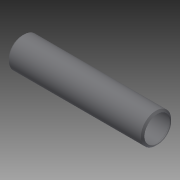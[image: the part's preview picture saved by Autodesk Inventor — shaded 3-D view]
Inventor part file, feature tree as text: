
AUTODESK INVENTOR PART (.ipt)
format: ipt  version: 2014 (Build 180170000, 170)  size: 122,368 bytes
history: native  units: in
note: dims shown in document units (in); Inventor stores cm internally (conversion verified against a paired STEP export)
features: other x56, revolve x1, sketch x1
ambient origin geometry x8: Origin, YZ Plane, XZ Plane, XY Plane, X Axis, Y Axis, Z Axis, Center Point
bodies: Solid1 (feature_tree)
feature tree (58):
  revolve  "Revolution1"  [1 undecoded]
  other  "o1_XY"
  other  "o1_YZ"
  other  "o1_ZX"
  other  "o1_X"
  other  "o1_Y"
  other  "o1_Z"
  other  "o1_Center"
  other  "o2_XY"
  other  "o2_YZ"
  other  "o2_ZX"
  other  "o2_X"
  other  "o2_Y"
  other  "o2_Z"
  other  "o2_Center"
  other  "t1_XY"
  other  "t1_YZ"
  other  "t1_ZX"
  other  "t1_X"
  other  "t1_Y"
  other  "t1_Z"
  other  "t1_Center"
  other  "t2_XY"
  other  "t2_YZ"
  other  "t2_ZX"
  other  "t2_X"
  other  "t2_Y"
  other  "t2_Z"
  other  "t2_Center"
  other  "t3_XY"
  other  "t3_YZ"
  other  "t3_ZX"
  other  "t3_X"
  other  "t3_Y"
  other  "t3_Z"
  other  "t3_Center"
  other  "t4_XY"
  other  "t4_YZ"
  other  "t4_ZX"
  other  "t4_X"
  other  "t4_Y"
  other  "t4_Z"
  other  "t4_Center"
  other  "tube1_XY"
  other  "tube1_YZ"
  other  "tube1_ZX"
  other  "tube1_X"
  other  "tube1_Y"
  other  "tube1_Z"
  other  "tube1_Center"
  other  "tube2_XY"
  other  "tube2_YZ"
  other  "tube2_ZX"
  other  "tube2_X"
  other  "tube2_Y"
  other  "tube2_Z"
  other  "tube2_Center"
  sketch  "Sketch_5"  dims[d0=360.0deg]
note: 1 required parameter value undecoded (feature->parameter linkage not recoverable at this tier; creation-order binding heuristic only, values carry confidence <= 0.55)
